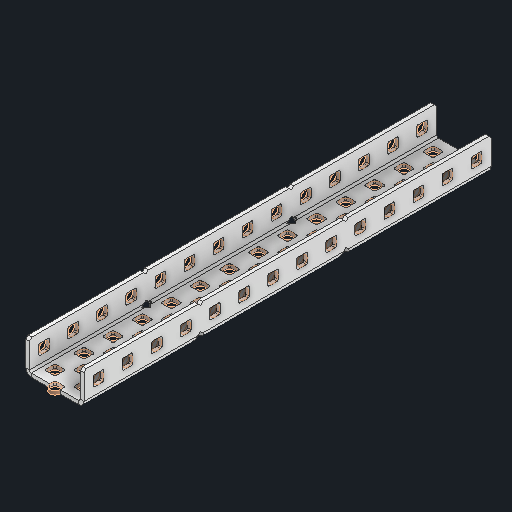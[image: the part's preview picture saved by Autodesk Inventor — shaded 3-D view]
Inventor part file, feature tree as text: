
AUTODESK INVENTOR PART (.ipt)
format: ipt  version: 2024 (Build 280153000, 153)  size: 1,234,944 bytes
history: native  units: in
note: dims shown in document units (in); Inventor stores cm internally (conversion verified against a paired STEP export)
features: other x146, sketch x5, sheet_metal_op x1
ambient origin geometry x8: Origin, YZ Plane, XZ Plane, XY Plane, X Axis, Y Axis, Z Axis, Center Point
bodies: Solid1 (feature_tree)
feature tree (152):
  other  "Alu C 1x2x1x14.ipt"
  other  "Solid1::Alu C 1x2x1x14.ipt"
  other  "TaggingFeature1"
  sketch  "Sketch1"  dims[d0=0.3937in]
  sketch  "Sketch2"  dims[d1=0.0625in]
  sketch  "Sketch3"
  other  "Flange Pattern Sketch"
  sketch  "Sketch9"
  sheet_metal_op  "Body Pattern Sketch"
  other  "Arc Length"
  sketch  "Sketch14"
  other  "Flange Pattern Plane"
  other  "Srf1"
  other  "Srf2"
  other  "Srf3"
  other  "Srf4"
  other  "Srf5"
  other  "Srf6"
  other  "Srf7"
  other  "Srf8"
  other  "Srf9"
  other  "Srf10"
  other  "Srf11"
  other  "Srf12"
  other  "Srf13"
  other  "Srf14"
  other  "Srf15"
  other  "Srf16"
  other  "Srf17"
  other  "Srf18"
  other  "Srf19"
  other  "Srf20"
  other  "Srf21"
  other  "Srf22"
  other  "Srf23"
  other  "Srf24"
  other  "Srf25"
  other  "Srf26"
  other  "Srf27"
  other  "Srf28"
  other  "Srf29"
  other  "Srf30"
  other  "Srf31"
  other  "Srf32"
  other  "Srf33"
  other  "Srf34"
  other  "Srf35"
  other  "Srf36"
  other  "Srf37"
  other  "Srf38"
  other  "Srf39"
  other  "Srf40"
  other  "Srf41"
  other  "Srf42"
  other  "Srf43"
  other  "Srf44"
  other  "Srf45"
  other  "Srf46"
  other  "Srf47"
  other  "Srf48"
  other  "Srf49"
  other  "Srf50"
  other  "Srf51"
  other  "Srf52"
  other  "Srf53"
  other  "Srf54"
  other  "Srf55"
  other  "Srf56"
  other  "Srf57"
  other  "Srf58"
  other  "Srf59"
  other  "Srf60"
  other  "Srf61"
  other  "Srf62"
  other  "Srf63"
  other  "Srf64"
  other  "Srf65"
  other  "Srf66"
  other  "Srf67"
  other  "Srf68"
  other  "Srf69"
  other  "Srf70"
  other  "Srf1::Derived"
  other  "Srf2::Derived"
  other  "Srf823::Derived"
  other  "Srf824::Derived"
  other  "Srf825::Derived"
  other  "Srf826::Derived"
  other  "Srf827::Derived"
  other  "Srf828::Derived"
  other  "Srf829::Derived"
  other  "Srf922::Derived"
  other  "Srf923::Derived"
  other  "Srf924::Derived"
  other  "Srf925::Derived"
  other  "Srf926::Derived"
  other  "Srf1143::Derived"
  other  "Srf1144::Derived"
  other  "Srf1145::Derived"
  other  "Srf1146::Derived"
  other  "Srf1147::Derived"
  other  "Srf1148::Derived"
  other  "Srf1149::Derived"
  other  "Srf1150::Derived"
  other  "Srf1151::Derived"
  other  "Srf1152::Derived"
  other  "Srf1153::Derived"
  other  "Srf1154::Derived"
  other  "Srf1155::Derived"
  other  "Srf1156::Derived"
  other  "Srf91::Derived"
  other  "Srf92::Derived"
  other  "Srf856::Derived"
  other  "Srf857::Derived"
  other  "Srf858::Derived"
  other  "Srf859::Derived"
  other  "Srf860::Derived"
  other  "Srf861::Derived"
  other  "Srf862::Derived"
  other  "Srf959::Derived"
  other  "Srf960::Derived"
  other  "Srf961::Derived"
  other  "Srf962::Derived"
  other  "Srf963::Derived"
  other  "Srf1199::Derived"
  other  "Srf1200::Derived"
  other  "Srf1201::Derived"
  other  "Srf1202::Derived"
  other  "Srf1203::Derived"
  other  "Srf1204::Derived"
  other  "Srf1205::Derived"
  other  "Srf1206::Derived"
  other  "Srf1207::Derived"
  other  "Srf1208::Derived"
  other  "Srf1209::Derived"
  other  "Srf1210::Derived"
  other  "Srf1211::Derived"
  other  "Srf1212::Derived"
  other  "Srf786::Derived"
  other  "Srf889::Derived"
  other  "Srf890::Derived"
  other  "Srf891::Derived"
  other  "Srf892::Derived"
  other  "Srf893::Derived"
  other  "Srf894::Derived"
  other  "Srf895::Derived"
  other  "Srf896::Derived"
  other  "Srf996::Derived"
  other  "Srf997::Derived"
  other  "Srf998::Derived"
  other  "Srf999::Derived"
  other  "Srf1000::Derived"
